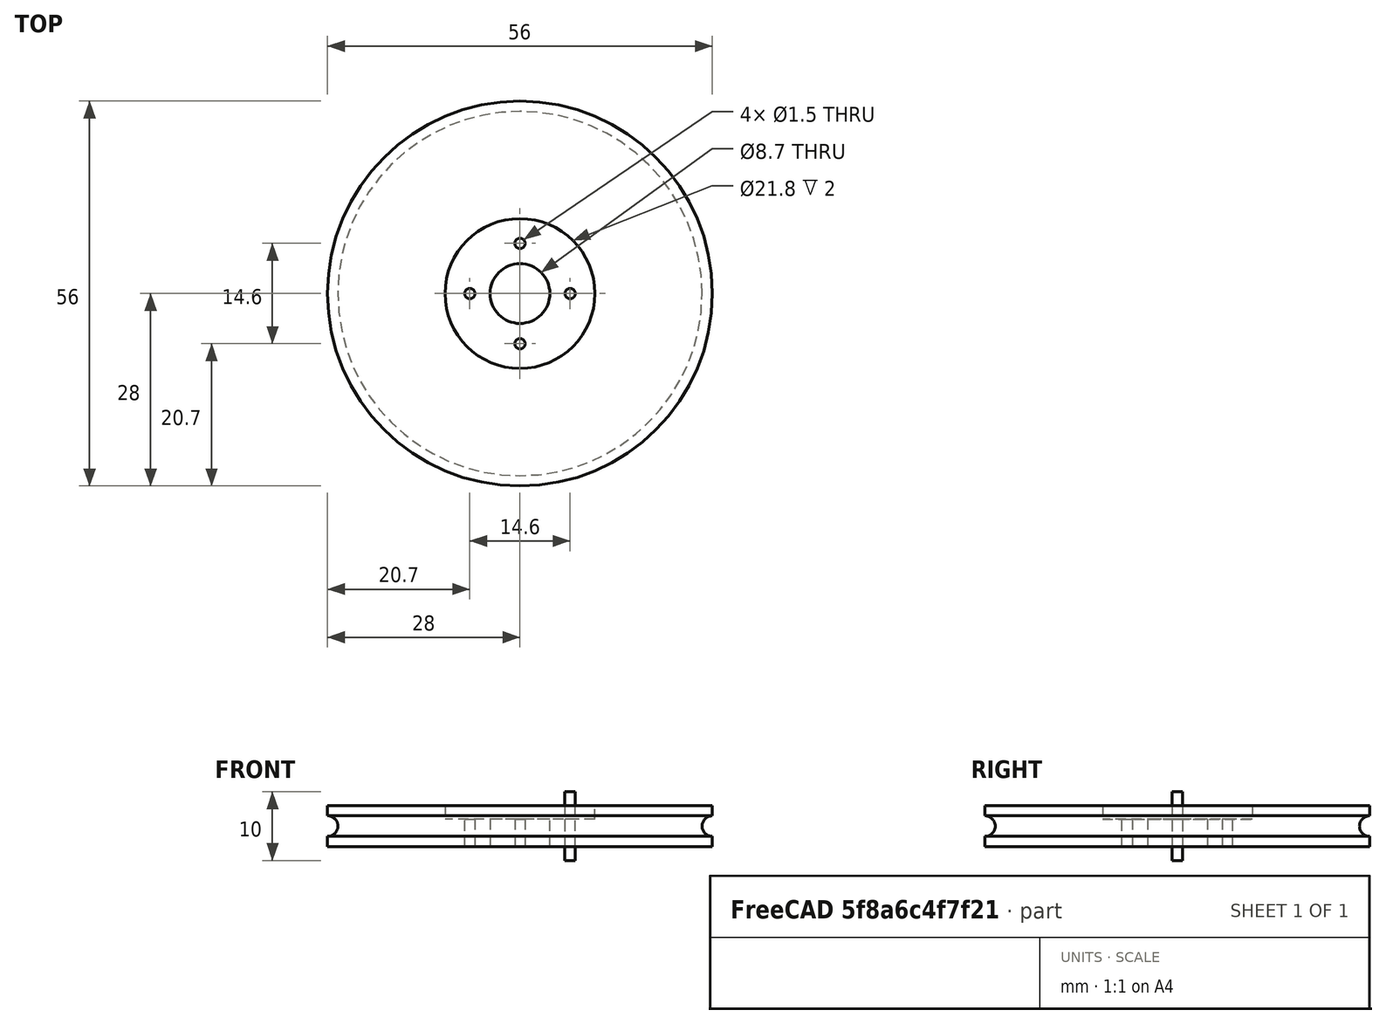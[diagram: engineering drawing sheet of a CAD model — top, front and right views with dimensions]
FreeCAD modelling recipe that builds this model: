
FCSTD DOCUMENT  (FreeCAD 1.0R39319 (Git))
Label: ojt1_t15p01_mini_skybot
License: All rights reserved
LicenseURL: https://en.wikipedia.org/wiki/All_rights_reserved
objects: Part::Cylinder×4, Part::Cut×4, Part::Torus×1, Part::FeaturePython×1
note: 9 computed .brp shape members not serialized (recipe doc carries the construction recipe); baked Part::Feature solids carry a one-line shape summary decoded from their .brp

FEATURE [Part::Cylinder] Cylinder  label="rueda base"
  Angle = 360
  AttacherType = Attacher::AttachEngine3D
  FirstAngle = 0
  Height = 6
  Placement = pos=(0,0,-3) rot=(0,0,1;0rad)
  Radius = 28
  SecondAngle = 0
FEATURE [Part::Torus] Torus  label="junta"
  Angle1 = -180
  Angle2 = 180
  Angle3 = 360
  AttacherType = Attacher::AttachEngine3D
  Radius1 = 28
  Radius2 = 1.5
FEATURE [Part::Cut] Cut
  Base = -> Cylinder
  Refine = true
  Tool = -> Torus
FEATURE [Part::Cylinder] Cylinder001  label="Cilindre"
  Angle = 360
  AttacherType = Attacher::AttachEngine3D
  FirstAngle = 0
  Height = 10
  Placement = pos=(0,0,1) rot=(0,0,1;0rad)
  Radius = 10.9
  SecondAngle = 0
FEATURE [Part::Cut] Cut001
  Base = -> Cut
  Refine = true
  Tool = -> Cylinder001
FEATURE [Part::Cylinder] Cylinder002  label="Cilindre001"
  Angle = 360
  AttacherType = Attacher::AttachEngine3D
  FirstAngle = 0
  Height = 10
  Placement = pos=(0,0,-4) rot=(0,0,1;0rad)
  Radius = 4.35
  SecondAngle = 0
FEATURE [Part::Cut] Cut002
  Base = -> Cut001
  Refine = true
  Tool = -> Cylinder002
FEATURE [Part::Cylinder] Cylinder003  label="Cilindre002"
  Angle = 360
  AttacherType = Attacher::AttachEngine3D
  FirstAngle = 0
  Height = 10
  Placement = pos=(7.3,0,-5) rot=(0,0,1;0rad)
  Radius = 0.75
  SecondAngle = 0
FEATURE [Part::FeaturePython] Array  # Draft array (typed FeaturePython)
  AlwaysSyncPlacement = false
  Angle = 360
  ArrayType = 1
  Axis = (0,0,1)
  Base = -> Cylinder003
  Center = (0,0,0)
  Count = 4
  ExpandArray = false
  Fuse = false
  IntervalAxis = (0,0,0)
  IntervalX = (10,0,0)
  IntervalY = (0,100,0)
  IntervalZ = (0,0,100)
  NumberCircles = 3
  NumberPolar = 4
  NumberX = 2
  NumberY = 2
  NumberZ = 1
  PlacementList = 4 placements: [(7.3,0,-5),(0,7.3,-5),(-7.3,8.93992e-16,-5),(-1.62093e-15,-7.3,-5)]
  RadialDistance = 50
  ScaleList = (4) [(1,1,1),(1,1,1),(1,1,1),(1,1,1)]
  Symmetry = 1
  TangentialDistance = 25
FEATURE [Part::Cut] Cut003
  Base = -> Cut002
  Refine = true
  Tool = -> Array
